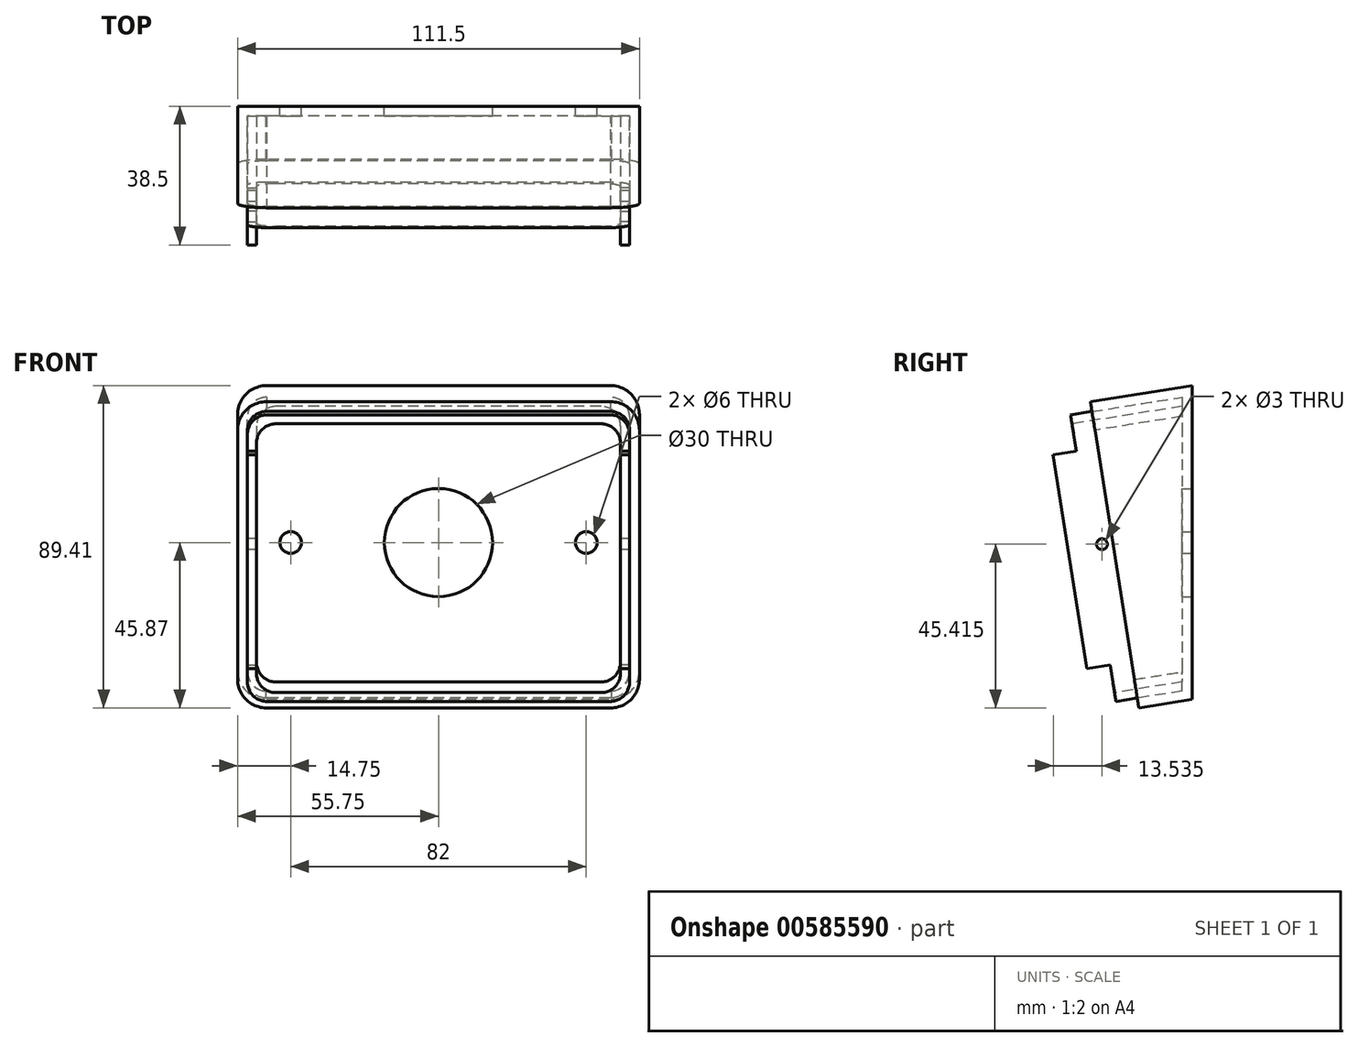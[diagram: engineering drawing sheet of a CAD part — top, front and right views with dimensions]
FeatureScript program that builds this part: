
annotation { "Feature Type Name" : "Feature", "Feature Type Description" : "" }
export const myFeature = defineFeature(function(context is Context, id is Id, definition is map)
    precondition{}
    {
        {
            var Q0;
            Q0=qCreatedBy(makeId("Front.planeOp"),FACE);
            cPlane(context, id + "F0", {"entities" : qUnion([Q0]), "cplaneType" : CPlaneType.OFFSET, "offset" : 22 * mm, "width" : 150 * mm, "height" : 150 * mm});
        }
        {
            var Q0;
            Q0=qCreatedBy(id+"F0.planeOp",FACE);
            var sketch = newSketch(context, id + "F1", { "sketchPlane" : qUnion([Q0])});
            skLineSegment(sketch, "E0", {"start": v(-67.43, 0) * mm, "end": v(64.52, 0) * mm});
            skSolve(sketch);
        }
        {
            var Q0;
            Q0=qCreatedBy(makeId("Front.planeOp"),FACE);
            var Q1;
            Q1=sQuery(id+"F1.wireOp",EDGE,"E0");
            cPlane(context, id + "F2", {"entities" : qUnion([Q0, Q1]), "cplaneType" : CPlaneType.LINE_ANGLE, "offset" : 15 * mm, "angle" : 9 * degree, "width" : 150 * mm, "height" : 150 * mm});
        }
        {
            var Q0;
            Q0=qCreatedBy(id+"F2.planeOp",FACE);
            var sketch = newSketch(context, id + "F3", { "sketchPlane" : qUnion([Q0])});
            skLineSegment(sketch, "E1.bottom", {"start": v(-47.75, 43) * mm, "end": v(47.75, 43) * mm});
            skLineSegment(sketch, "E1.top", {"start": v(-47.75, -43) * mm, "end": v(47.75, -43) * mm});
            skLineSegment(sketch, "E1.left", {"start": v(-55.75, 35) * mm, "end": v(-55.75, -35) * mm});
            skLineSegment(sketch, "E1.right", {"start": v(55.75, 35) * mm, "end": v(55.75, -35) * mm});
            skPoint(sketch, "E1.middle", {"position": v(0, 0) * mm});
            skPoint(sketch, "E2.visualSharp", {"position": v(-55.75, 43) * mm});
            skArc(sketch, "E2.filletArc", {"start": v(-47.75, 43) * mm, "mid": v(-53.4, 40.66) * mm, "end": v(-55.75, 35) * mm});
            skPoint(sketch, "E3.visualSharp", {"position": v(55.75, 43) * mm});
            skArc(sketch, "E3.filletArc", {"start": v(55.75, 35) * mm, "mid": v(53.4, 40.66) * mm, "end": v(47.75, 43) * mm});
            skPoint(sketch, "E4.visualSharp", {"position": v(55.75, -43) * mm});
            skArc(sketch, "E4.filletArc", {"start": v(47.75, -43) * mm, "mid": v(53.4, -40.66) * mm, "end": v(55.75, -35) * mm});
            skPoint(sketch, "E5.visualSharp", {"position": v(-55.75, -43) * mm});
            skArc(sketch, "E5.filletArc", {"start": v(-55.75, -35) * mm, "mid": v(-53.4, -40.66) * mm, "end": v(-47.75, -43) * mm});
            skSolve(sketch);
        }
        {
            var Q0;
            Q0=qSketchRegion(id+"F3",true);
            var Q1;
            Q1=qCreatedBy(makeId("Front.planeOp"),FACE);
            extrude(context, id + "F4", {"entities" : qUnion([Q0]), "endBound" : BoundingType.UP_TO_SURFACE, "endBoundEntityFace" : qUnion([Q1]), "depth" : 20 * mm, "offsetDistance" : 25 * mm});
        }
        {
            var Q0;
            Q0=makeQuery(id+"F4.opExtrude","CAP_FACE",FACE,{"disambiguationData":[OSD([sQuery(id+"F3.wireOp",EDGE,"E1.bottom"),sQuery(id+"F3.wireOp",EDGE,"E1.top"),sQuery(id+"F3.wireOp",EDGE,"E1.left"),sQuery(id+"F3.wireOp",EDGE,"E1.right"),sQuery(id+"F3.wireOp",EDGE,"E2.filletArc"),sQuery(id+"F3.wireOp",EDGE,"E3.filletArc"),sQuery(id+"F3.wireOp",EDGE,"E4.filletArc"),sQuery(id+"F3.wireOp",EDGE,"E5.filletArc")])],"isStart":true});
            shell(context, id + "F5", {"entities" : qUnion([Q0]), "thickness" : 2.75 * mm});
        }
        {
            var Q0;
            Q0=qCreatedBy(makeId("Front.planeOp"),FACE);
            var sketch = newSketch(context, id + "F6", { "sketchPlane" : qUnion([Q0])});
            skCircle(sketch, "E6", {"center": v(0, 0) * mm, "radius": 15 * mm});
            skCircle(sketch, "E7", {"center": v(-41, 0) * mm, "radius": 3 * mm});
            skCircle(sketch, "E8.MirrorC", {"center": v(41, 0) * mm, "radius": 3 * mm});
            skSolve(sketch);
        }
        {
            var Q0;
            Q0=qSketchRegion(id+"F6",true);
            extrude(context, id + "F7", {"entities" : qUnion([Q0]), "operationType" : NewBodyOperationType.REMOVE, "depth" : 25 * mm, "offsetDistance" : 25 * mm});
        }
        {
            var Q0;
            Q0=qCreatedBy(id+"F2.planeOp",FACE);
            cPlane(context, id + "F8", {"entities" : qUnion([Q0]), "cplaneType" : CPlaneType.OFFSET, "offset" : 6 * mm, "oppositeDirection" : true, "width" : 150 * mm, "height" : 150 * mm});
        }
        {
            var Q0;
            Q0=qCreatedBy(id+"F8.planeOp",FACE);
            var sketch = newSketch(context, id + "F9", { "sketchPlane" : qUnion([Q0])});
            skLineSegment(sketch, "E9.bottom", {"start": v(-47.6, 40.24) * mm, "end": v(47.6, 40.24) * mm});
            skLineSegment(sketch, "E9.top", {"start": v(-47.6, -40.26) * mm, "end": v(47.6, -40.26) * mm});
            skLineSegment(sketch, "E9.left", {"start": v(-53, 34.84) * mm, "end": v(-53, -34.86) * mm});
            skLineSegment(sketch, "E9.right", {"start": v(53, 34.84) * mm, "end": v(53, -34.86) * mm});
            skPoint(sketch, "E9.middle", {"position": v(0, 0) * mm});
            skPoint(sketch, "E10.visualSharp", {"position": v(-53, 40.24) * mm});
            skArc(sketch, "E10.filletArc", {"start": v(-47.6, 40.24) * mm, "mid": v(-51.42, 38.66) * mm, "end": v(-53, 34.84) * mm});
            skPoint(sketch, "E11.visualSharp", {"position": v(53, 40.24) * mm});
            skArc(sketch, "E11.filletArc", {"start": v(53, 34.84) * mm, "mid": v(51.42, 38.66) * mm, "end": v(47.6, 40.24) * mm});
            skPoint(sketch, "E12.visualSharp", {"position": v(53, -40.26) * mm});
            skArc(sketch, "E12.filletArc", {"start": v(47.6, -40.26) * mm, "mid": v(51.42, -38.68) * mm, "end": v(53, -34.86) * mm});
            skPoint(sketch, "E13.visualSharp", {"position": v(-53, -40.26) * mm});
            skArc(sketch, "E13.filletArc", {"start": v(-53, -34.86) * mm, "mid": v(-51.42, -38.68) * mm, "end": v(-47.6, -40.26) * mm});
            skLineSegment(sketch, "E14.bottom", {"start": v(-45.1, 37.74) * mm, "end": v(45.1, 37.74) * mm});
            skLineSegment(sketch, "E14.top", {"start": v(-45.1, -37.76) * mm, "end": v(45.1, -37.76) * mm});
            skLineSegment(sketch, "E14.left", {"start": v(-50.5, 32.34) * mm, "end": v(-50.5, -32.36) * mm});
            skLineSegment(sketch, "E14.right", {"start": v(50.5, 32.34) * mm, "end": v(50.5, -32.36) * mm});
            skPoint(sketch, "E15.visualSharp", {"position": v(-50.5, 37.74) * mm});
            skArc(sketch, "E15.filletArc", {"start": v(-45.1, 37.74) * mm, "mid": v(-48.92, 36.16) * mm, "end": v(-50.5, 32.34) * mm});
            skPoint(sketch, "E16.visualSharp", {"position": v(50.5, 37.74) * mm});
            skArc(sketch, "E16.filletArc", {"start": v(50.5, 32.34) * mm, "mid": v(48.92, 36.16) * mm, "end": v(45.1, 37.74) * mm});
            skPoint(sketch, "E17.visualSharp", {"position": v(50.5, -37.76) * mm});
            skArc(sketch, "E17.filletArc", {"start": v(45.1, -37.76) * mm, "mid": v(48.92, -36.18) * mm, "end": v(50.5, -32.36) * mm});
            skPoint(sketch, "E18.visualSharp", {"position": v(-50.5, -37.76) * mm});
            skArc(sketch, "E18.filletArc", {"start": v(-50.5, -32.36) * mm, "mid": v(-48.92, -36.18) * mm, "end": v(-45.1, -37.76) * mm});
            skSolve(sketch);
        }
        {
            var Q0;
            Q0=qSketchRegion(id+"F9",true);
            var Q1;
            Q1=qCreatedBy(makeId("Front.planeOp"),FACE);
            extrude(context, id + "F10", {"entities" : qUnion([Q0]), "operationType" : NewBodyOperationType.ADD, "endBound" : BoundingType.UP_TO_SURFACE, "depth" : 25 * mm, "endBoundEntityFace" : qUnion([Q1]), "offsetDistance" : 25 * mm});
        }
        {
            var Q0;
            Q0=qCreatedBy(id+"F2.planeOp",FACE);
            cPlane(context, id + "F11", {"entities" : qUnion([Q0]), "cplaneType" : CPlaneType.OFFSET, "offset" : 12.5 * mm, "oppositeDirection" : true, "width" : 150 * mm, "height" : 150 * mm});
        }
        {
            var Q0;
            Q0=qCreatedBy(makeId("Front.planeOp"),FACE);
            cPlane(context, id + "F12", {"entities" : qUnion([Q0]), "cplaneType" : CPlaneType.OFFSET, "offset" : 2.5 * mm, "width" : 150 * mm, "height" : 150 * mm});
        }
        {
            var Q0;
            Q0=sQuery(id+"F1.wireOp",EDGE,"E0");
            cPlane(context, id + "F13", {"entities" : qUnion([Q0]), "cplaneType" : CPlaneType.LINE_ANGLE, "offset" : 25 * mm, "angle" : 81 * degree, "oppositeDirection" : true, "width" : 150 * mm, "height" : 150 * mm});
        }
        {
            var Q0;
            Q0=qCreatedBy(id+"F11.planeOp",FACE);
            var sketch = newSketch(context, id + "F14", { "sketchPlane" : qUnion([Q0])});
            skLineSegment(sketch, "E19.bottom", {"start": v(50.5, 30) * mm, "end": v(53, 30) * mm});
            skLineSegment(sketch, "E19.top", {"start": v(50.5, -30) * mm, "end": v(53, -30) * mm});
            skLineSegment(sketch, "E19.left", {"start": v(50.5, 30) * mm, "end": v(50.5, -30) * mm});
            skLineSegment(sketch, "E19.right", {"start": v(53, 30) * mm, "end": v(53, -30) * mm});
            skPoint(sketch, "E19.middle", {"position": v(51.75, 0) * mm});
            skLineSegment(sketch, "E20.MirrorCS", {"start": v(-53, 30) * mm, "end": v(-53, -30) * mm});
            skLineSegment(sketch, "E21.MirrorCS", {"start": v(-50.5, 30) * mm, "end": v(-50.5, -30) * mm});
            skLineSegment(sketch, "E22.MirrorCS", {"start": v(-50.5, 30) * mm, "end": v(-53, 30) * mm});
            skLineSegment(sketch, "E23.MirrorCS", {"start": v(-50.5, -30) * mm, "end": v(-53, -30) * mm});
            skSolve(sketch);
        }
        {
            var Q0;
            Q0=qSketchRegion(id+"F14",true);
            var Q1;
            Q1=qCreatedBy(makeId("Front.planeOp"),FACE);
            extrude(context, id + "F15", {"entities" : qUnion([Q0]), "operationType" : NewBodyOperationType.ADD, "endBound" : BoundingType.UP_TO_SURFACE, "depth" : 25 * mm, "endBoundEntityFace" : qUnion([Q1]), "offsetDistance" : 25 * mm});
        }
        {
            var Q0;
            Q0=qCreatedBy(makeId("Right.planeOp"),FACE);
            var sketch = newSketch(context, id + "F16", { "sketchPlane" : qUnion([Q0])});
            skCircle(sketch, "E24", {"center": v(-24.97, -0.46) * mm, "radius": 1.5 * mm});
            skSolve(sketch);
        }
        {
            var Q0;
            Q0=qSketchRegion(id+"F16",true);
            extrude(context, id + "F17", {"entities" : qUnion([Q0]), "operationType" : NewBodyOperationType.REMOVE, "endBound" : BoundingType.SYMMETRIC, "depth" : 140 * mm, "offsetDistance" : 25 * mm});
        }
    });
